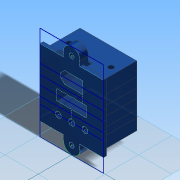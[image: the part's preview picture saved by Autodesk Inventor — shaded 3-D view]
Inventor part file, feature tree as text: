
AUTODESK INVENTOR PART (.ipt)
format: ipt  version: 2014 SP2 (Build 180246200, 246)  size: 378,368 bytes
history: native  units: in
note: dims shown in document units (in); Inventor stores cm internally (conversion verified against a paired STEP export)
features: extrude x6, boolean_combine x6, other x3, sketch x1, projected_geometry x1
ambient origin geometry x8: Origin, YZ Plane, XZ Plane, XY Plane, X Axis, Y Axis, Z Axis, Center Point
bodies: Solid2 (feature_tree), Solid3 (feature_tree), Solid4 (feature_tree), Solid5 (feature_tree), Solid6 (feature_tree), Solid7 (feature_tree), Solid1 (feature_tree)
feature tree (17):
  other  "PanelMountNew.ipt"
  sketch  "Sketch1"  dims[d0=0.3937in d1=2.0in d2=0.0in d3=2.0in d4=0.0in d5=2.0in d6=0.0in d7=2.0in d8=0.0in d9=2.0in d10=0.0in d11=2.0in d12=0.0in]
  extrude  "Extrusion1"  Depth=0.3937in TaperAngle=0.0deg
  extrude  "Extrusion2"  Depth=0.3937in TaperAngle=0.0deg
  extrude  "Extrusion3"  Depth=0.3937in TaperAngle=0.0deg
  extrude  "Extrusion4"  Depth=0.3937in TaperAngle=0.0deg
  extrude  "Extrusion5"  Depth=0.3937in TaperAngle=0.0deg
  extrude  "Extrusion6"  Depth=0.3937in TaperAngle=0.0deg
  boolean_combine  "Combine1"
  boolean_combine  "Combine2"
  boolean_combine  "Combine3"
  boolean_combine  "Combine4"
  boolean_combine  "Combine5"
  boolean_combine  "Combine6"
  other  "Solid1::PanelMountNew.ipt"
  other  "TaggingFeature1"
  projected_geometry  "Projected Loop1"
